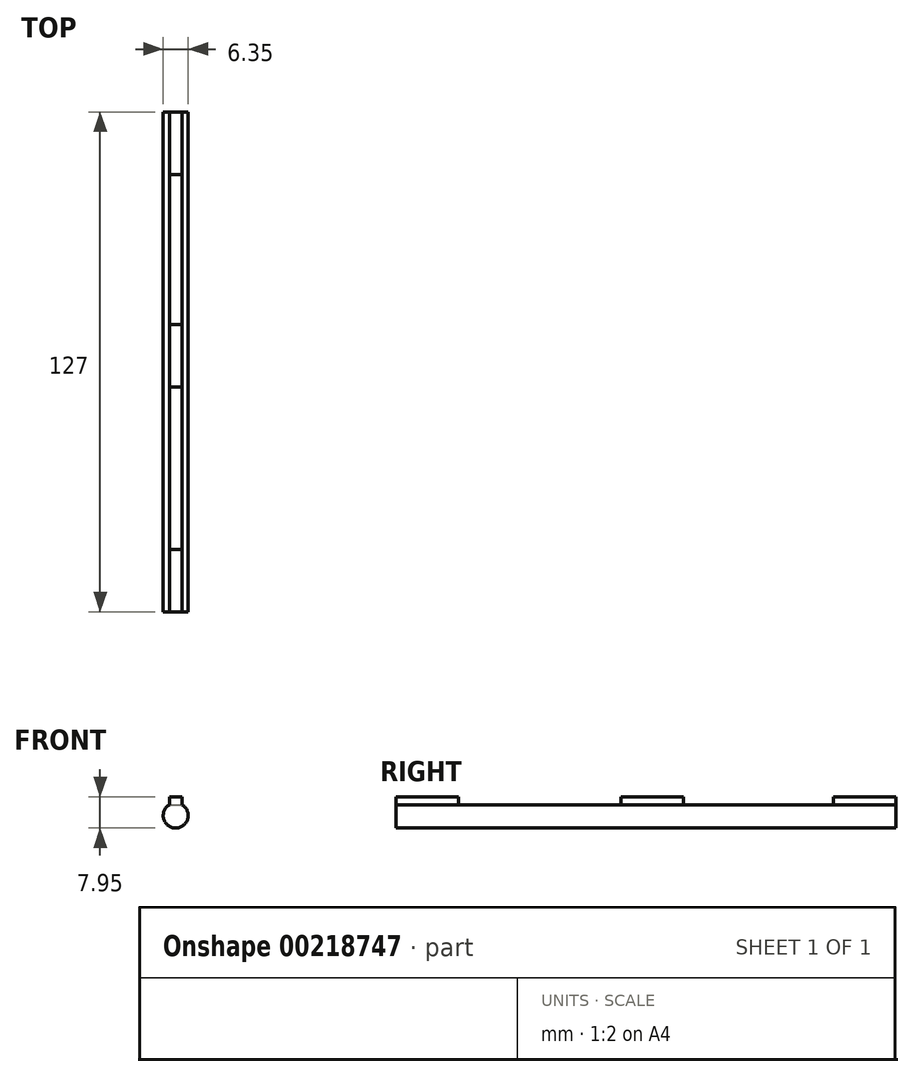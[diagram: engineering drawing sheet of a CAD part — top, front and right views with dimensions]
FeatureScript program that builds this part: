
annotation { "Feature Type Name" : "Feature", "Feature Type Description" : "" }
export const myFeature = defineFeature(function(context is Context, id is Id, definition is map)
    precondition{}
    {
        {
            var Q0;
            Q0=qCreatedBy(makeId("Front.planeOp"),FACE);
            var sketch = newSketch(context, id + "F0", { "sketchPlane" : qUnion([Q0])});
            skArc(sketch, "E0", {"start": v(-1.59, 2.75) * mm, "mid": v(0, -3.18) * mm, "end": v(1.59, 2.75) * mm});
            skLineSegment(sketch, "E1", {"start": v(-1.59, 4.78) * mm, "end": v(1.59, 4.78) * mm});
            skLineSegment(sketch, "E2", {"start": v(1.59, 4.78) * mm, "end": v(1.59, 2.75) * mm});
            skLineSegment(sketch, "E3.MirrorCS", {"start": v(-1.59, 4.78) * mm, "end": v(-1.59, 2.75) * mm});
            skSolve(sketch);
        }
        {
            var Q0;
            Q0=makeQuery(id+"F0.imprint","IMPRINT",FACE,{"disambiguationData":[TD([[makeQuery(id+"F0.imprint","IMPRINT",EDGE,{"derivedFrom":sQuery(id+"F0.wireOp",EDGE,"E0")}),1.0]])]});
            extrude(context, id + "F1", {"entities" : qUnion([Q0]), "depth" : 127 * mm});
        }
        {
            var Q0;
            Q0=makeQuery(id+"F1.opExtrude","SWEPT_FACE",FACE,{"disambiguationData":[OSD([sQuery(id+"F0.wireOp",EDGE,"E2")])]});
            var sketch = newSketch(context, id + "F2", { "sketchPlane" : qUnion([Q0])});
            skLineSegment(sketch, "E4", {"start": v(-127, 4.78) * mm, "end": v(-111.12, 4.78) * mm});
            skLineSegment(sketch, "E5", {"start": v(-127, 2.75) * mm, "end": v(-127, 4.78) * mm});
            skLineSegment(sketch, "E6.0", {"start": v(-127, 2.74) * mm, "end": v(-111.12, 2.74) * mm});
            skLineSegment(sketch, "E7", {"start": v(-111.12, 2.74) * mm, "end": v(-111.12, 4.78) * mm});
            skLineSegment(sketch, "E8.0", {"start": v(-53.97, 2.74) * mm, "end": v(-69.85, 2.74) * mm});
            skLineSegment(sketch, "E9", {"start": v(-69.85, 2.74) * mm, "end": v(-69.85, 4.78) * mm});
            skLineSegment(sketch, "E10", {"start": v(-53.97, 2.74) * mm, "end": v(-53.97, 4.78) * mm});
            skLineSegment(sketch, "E11", {"start": v(-69.85, 4.78) * mm, "end": v(-53.97, 4.78) * mm});
            skPoint(sketch, "E12.endSnap0", {"position": v(-63.5, 4.78) * mm});
            skLineSegment(sketch, "E13", {"start": v(0, 4.78) * mm, "end": v(-15.88, 4.78) * mm});
            skLineSegment(sketch, "E14.0", {"start": v(0, 2.74) * mm, "end": v(-15.88, 2.74) * mm});
            skLineSegment(sketch, "E15", {"start": v(-15.88, 2.74) * mm, "end": v(-15.88, 4.78) * mm});
            skLineSegment(sketch, "E16", {"start": v(0, 2.75) * mm, "end": v(0, 4.78) * mm});
            skSolve(sketch);
        }
        {
            var Q0;
            {var subQ0=sQuery(id+"F2.wireOp",EDGE,"E7");var subQ1=sQuery(id+"F0.wireOp",EDGE,"E2");var subQ4=makeQuery(id+"F1.opExtrude","SWEPT_EDGE",EDGE,{"disambiguationData":[OSD([sQuery(id+"F0.wireOp",EDGE,"E0"),subQ1])]});var subQ5=makeQuery(id+"F2.imprint","INTERSECT",VERTEX,{"derivedFrom":[subQ4,subQ0]});Q0=makeQuery(id+"F2.imprint","IMPRINT",FACE,{"disambiguationData":[TD([[makeQuery(id+"F2.imprint","IMPRINT",EDGE,{"disambiguationData":[TD([[subQ5,-1.0]])],"derivedFrom":subQ0}),-1.0]])]});}
            var Q1;
            {var subQ0=sQuery(id+"F2.wireOp",EDGE,"E10");var subQ1=sQuery(id+"F0.wireOp",EDGE,"E2");var subQ4=makeQuery(id+"F1.opExtrude","SWEPT_EDGE",EDGE,{"disambiguationData":[OSD([sQuery(id+"F0.wireOp",EDGE,"E0"),subQ1])]});var subQ5=makeQuery(id+"F2.imprint","INTERSECT",VERTEX,{"derivedFrom":[subQ4,subQ0]});Q1=makeQuery(id+"F2.imprint","IMPRINT",FACE,{"disambiguationData":[TD([[makeQuery(id+"F2.imprint","IMPRINT",EDGE,{"disambiguationData":[TD([[subQ5,-1.0]])],"derivedFrom":subQ0}),-1.0]])]});}
            extrude(context, id + "F3", {"entities" : qUnion([Q0, Q1]), "operationType" : NewBodyOperationType.REMOVE, "oppositeDirection" : true, "depth" : 3.17 * mm});
        }
    });
